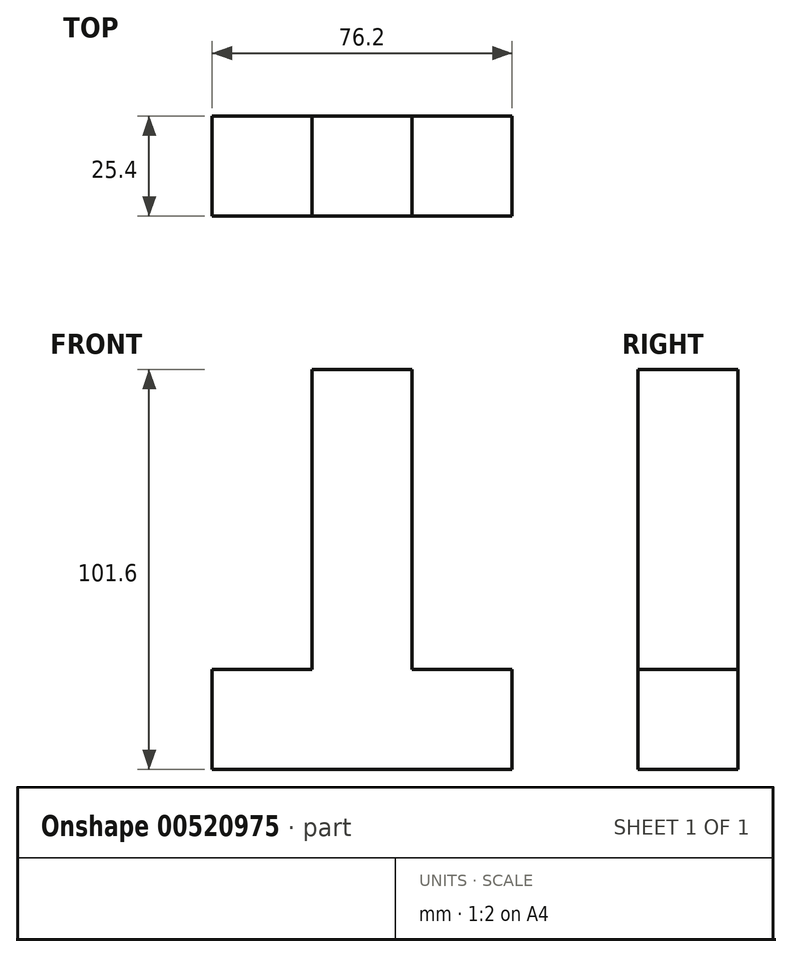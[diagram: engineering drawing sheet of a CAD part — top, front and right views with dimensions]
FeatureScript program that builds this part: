
annotation { "Feature Type Name" : "Feature", "Feature Type Description" : "" }
export const myFeature = defineFeature(function(context is Context, id is Id, definition is map)
    precondition{}
    {
        {
            var Q0;
            Q0=qCreatedBy(makeId("Front.planeOp"),FACE);
            var sketch = newSketch(context, id + "F0", { "sketchPlane" : qUnion([Q0])});
            skLineSegment(sketch, "E0", {"start": v(-76.2, 0) * mm, "end": v(-76.2, -101.6) * mm});
            skLineSegment(sketch, "E1", {"start": v(-76.2, -101.6) * mm, "end": v(0, -101.6) * mm});
            skLineSegment(sketch, "E2", {"start": v(0, -101.6) * mm, "end": v(0, 0) * mm});
            skLineSegment(sketch, "E3", {"start": v(0, 0) * mm, "end": v(-76.2, 0) * mm});
            skSolve(sketch);
        }
        {
            var Q0;
            Q0=makeQuery(id+"F0.imprint","IMPRINT",FACE,{"disambiguationData":[TD([[makeQuery(id+"F0.imprint","IMPRINT",EDGE,{"derivedFrom":sQuery(id+"F0.wireOp",EDGE,"E0")}),1.0]])]});
            extrude(context, id + "F1", {"entities" : qUnion([Q0]), "depth" : 25.4 * mm, "offsetDistance" : 25.4 * mm});
        }
        {
            var Q0;
            Q0=qCreatedBy(makeId("Front.planeOp"),FACE);
            var sketch = newSketch(context, id + "F2", { "sketchPlane" : qUnion([Q0])});
            skLineSegment(sketch, "E4", {"start": v(-76.2, 0) * mm, "end": v(-50.8, 0) * mm});
            skLineSegment(sketch, "E5", {"start": v(-50.8, 0) * mm, "end": v(-50.8, -76.2) * mm});
            skLineSegment(sketch, "E6", {"start": v(-50.8, -76.2) * mm, "end": v(-76.2, -76.2) * mm});
            skLineSegment(sketch, "E7", {"start": v(-76.2, -76.2) * mm, "end": v(-76.2, 0) * mm});
            skLineSegment(sketch, "E8", {"start": v(0, 0) * mm, "end": v(0, -76.2) * mm});
            skLineSegment(sketch, "E9", {"start": v(0, -76.2) * mm, "end": v(-25.4, -76.2) * mm});
            skLineSegment(sketch, "E10", {"start": v(-25.4, -76.2) * mm, "end": v(-25.4, 0) * mm});
            skLineSegment(sketch, "E11", {"start": v(-25.4, 0) * mm, "end": v(0, 0) * mm});
            skSolve(sketch);
        }
        {
            var Q0;
            Q0 = qSketchRegion(id + "F2", true);
            extrude(context, id + "F3", {"entities" : qUnion([Q0]), "operationType" : NewBodyOperationType.REMOVE, "depth" : 25.4 * mm, "offsetDistance" : 25.4 * mm});
        }
    });
